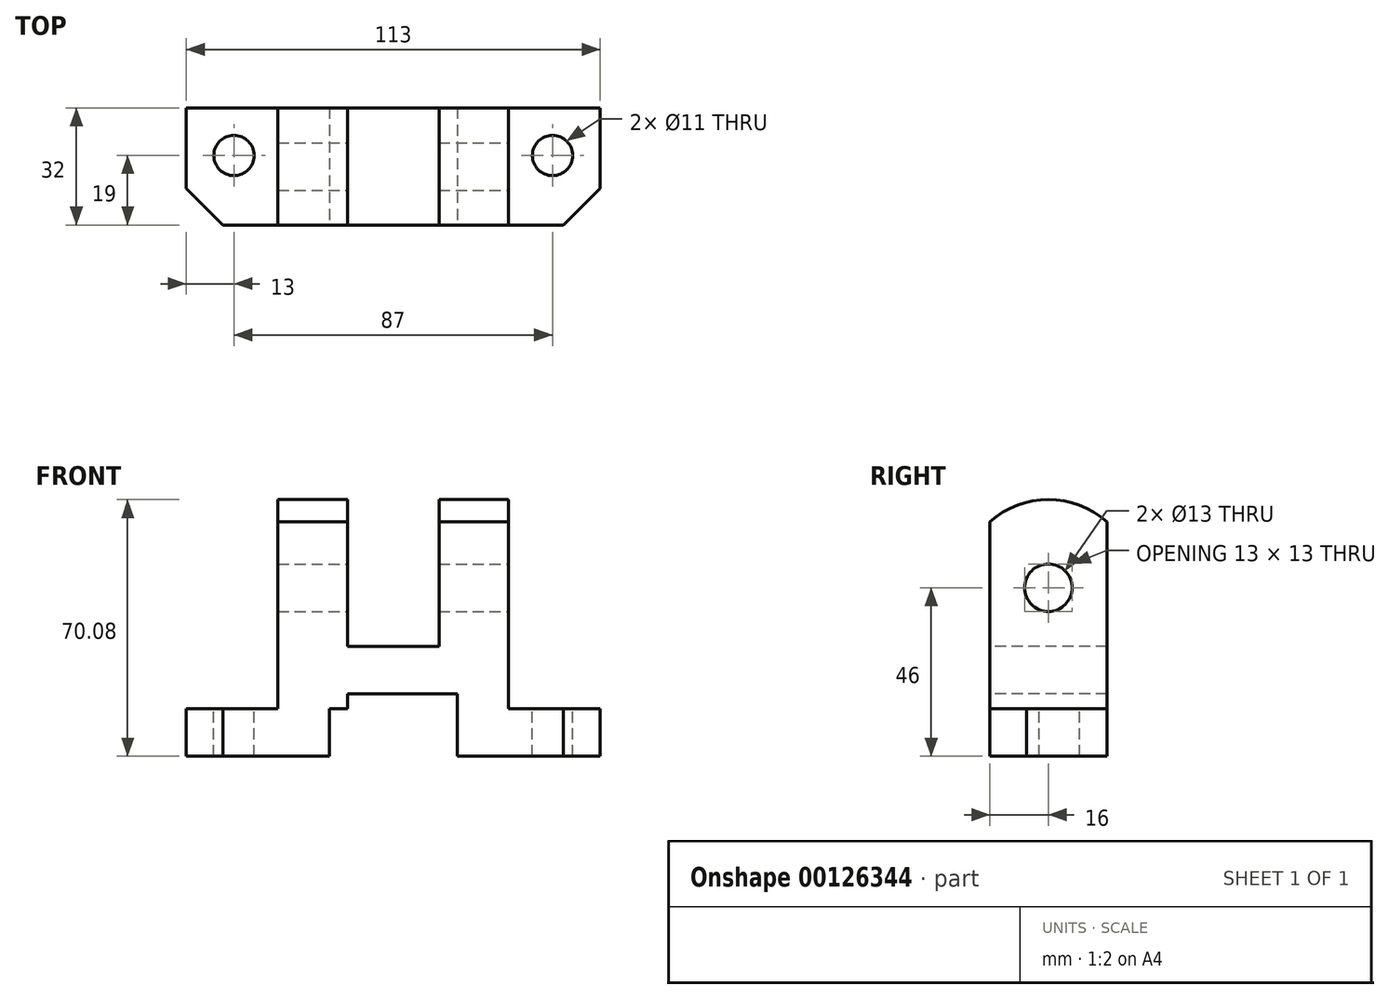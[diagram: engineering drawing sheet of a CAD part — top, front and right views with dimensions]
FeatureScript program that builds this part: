
annotation { "Feature Type Name" : "Feature", "Feature Type Description" : "" }
export const myFeature = defineFeature(function(context is Context, id is Id, definition is map)
    precondition{}
    {
        {
            var Q0;
            Q0=qCreatedBy(makeId("Front.planeOp"),FACE);
            var sketch = newSketch(context, id + "F0", { "sketchPlane" : qUnion([Q0])});
            skLineSegment(sketch, "E0", {"start": v(0, 0) * mm, "end": v(0, 13) * mm});
            skLineSegment(sketch, "E1", {"start": v(0, 13) * mm, "end": v(25, 13) * mm});
            skLineSegment(sketch, "E2", {"start": v(25, 13) * mm, "end": v(25, 64) * mm});
            skLineSegment(sketch, "E3", {"start": v(25, 64) * mm, "end": v(44, 64) * mm});
            skLineSegment(sketch, "E4", {"start": v(44, 64) * mm, "end": v(44, 30) * mm});
            skLineSegment(sketch, "E5", {"start": v(44, 30) * mm, "end": v(69, 30) * mm});
            skLineSegment(sketch, "E6", {"start": v(69, 30) * mm, "end": v(69, 64) * mm});
            skLineSegment(sketch, "E7", {"start": v(69, 64) * mm, "end": v(88, 64) * mm});
            skLineSegment(sketch, "E8", {"start": v(88, 64) * mm, "end": v(88, 13) * mm});
            skLineSegment(sketch, "E9", {"start": v(88, 13) * mm, "end": v(113, 13) * mm});
            skLineSegment(sketch, "E10", {"start": v(113, 13) * mm, "end": v(113, 0) * mm});
            skLineSegment(sketch, "E11", {"start": v(113, 0) * mm, "end": v(74, 0) * mm});
            skLineSegment(sketch, "E12", {"start": v(74, 0) * mm, "end": v(74, 17) * mm});
            skLineSegment(sketch, "E13", {"start": v(74, 17) * mm, "end": v(39, 17) * mm});
            skLineSegment(sketch, "E14", {"start": v(39, 17) * mm, "end": v(39, 0) * mm});
            skLineSegment(sketch, "E15", {"start": v(39, 0) * mm, "end": v(0, 0) * mm});
            skSolve(sketch);
        }
        {
            var Q0;
            Q0=makeQuery(id+"F0.imprint","IMPRINT",FACE,{"disambiguationData":[TD([[makeQuery(id+"F0.imprint","IMPRINT",EDGE,{"derivedFrom":sQuery(id+"F0.wireOp",EDGE,"E0")}),-1.0]])]});
            extrude(context, id + "F1", {"entities" : qUnion([Q0]), "oppositeDirection" : true, "depth" : 32 * mm});
        }
        {
            var Q0;
            Q0=makeQuery(id+"F1.opExtrude","SWEPT_FACE",FACE,{"disambiguationData":[OSD([sQuery(id+"F0.wireOp",EDGE,"E9")])]});
            var sketch = newSketch(context, id + "F2", { "sketchPlane" : qUnion([Q0])});
            skLineSegment(sketch, "E16", {"start": v(103, 0) * mm, "end": v(113, 10) * mm});
            skLineSegment(sketch, "E17", {"start": v(113, 10) * mm, "end": v(113, 0) * mm});
            skLineSegment(sketch, "E18", {"start": v(113, 0) * mm, "end": v(103, 0) * mm});
            skSolve(sketch);
        }
        {
            var Q0;
            Q0=makeQuery(id+"F2.imprint","IMPRINT",FACE,{"disambiguationData":[TD([[makeQuery(id+"F2.imprint","IMPRINT",EDGE,{"derivedFrom":sQuery(id+"F2.wireOp",EDGE,"E16")}),-1.0]])]});
            extrude(context, id + "F3", {"entities" : qUnion([Q0]), "operationType" : NewBodyOperationType.REMOVE, "endBound" : BoundingType.THROUGH_ALL, "oppositeDirection" : true, "depth" : 25 * mm});
        }
        {
            var Q0;
            Q0=makeQuery(id+"F1.opExtrude","SWEPT_FACE",FACE,{"disambiguationData":[OSD([sQuery(id+"F0.wireOp",EDGE,"E1")])]});
            var sketch = newSketch(context, id + "F4", { "sketchPlane" : qUnion([Q0])});
            skLineSegment(sketch, "E19", {"start": v(0, 0) * mm, "end": v(0, 10) * mm});
            skLineSegment(sketch, "E20", {"start": v(0, 10) * mm, "end": v(10, 0) * mm});
            skLineSegment(sketch, "E21", {"start": v(10, 0) * mm, "end": v(0, 0) * mm});
            skSolve(sketch);
        }
        {
            var Q0;
            Q0=makeQuery(id+"F4.imprint","IMPRINT",FACE,{"disambiguationData":[TD([[makeQuery(id+"F4.imprint","IMPRINT",EDGE,{"derivedFrom":sQuery(id+"F4.wireOp",EDGE,"E19")}),1.0]])]});
            extrude(context, id + "F5", {"entities" : qUnion([Q0]), "operationType" : NewBodyOperationType.REMOVE, "endBound" : BoundingType.THROUGH_ALL, "oppositeDirection" : true, "depth" : 25 * mm});
        }
        {
            var Q0;
            Q0=makeQuery(id+"F1.opExtrude","SWEPT_FACE",FACE,{"disambiguationData":[OSD([sQuery(id+"F0.wireOp",EDGE,"E9")])]});
            var sketch = newSketch(context, id + "F6", { "sketchPlane" : qUnion([Q0])});
            skCircle(sketch, "E22", {"center": v(100, 19) * mm, "radius": 5.5 * mm});
            skCircle(sketch, "E23", {"center": v(13, 19) * mm, "radius": 5.5 * mm});
            skSolve(sketch);
        }
        {
            var Q0;
            Q0=makeQuery(id+"F6.imprint","IMPRINT",FACE,{"disambiguationData":[TD([[makeQuery(id+"F6.imprint","IMPRINT",EDGE,{"derivedFrom":sQuery(id+"F6.wireOp",EDGE,"E23")}),1.0]])]});
            var Q1;
            Q1=makeQuery(id+"F6.imprint","IMPRINT",FACE,{"disambiguationData":[TD([[makeQuery(id+"F6.imprint","IMPRINT",EDGE,{"derivedFrom":sQuery(id+"F6.wireOp",EDGE,"E22")}),1.0]])]});
            extrude(context, id + "F7", {"entities" : qUnion([Q0, Q1]), "operationType" : NewBodyOperationType.REMOVE, "endBound" : BoundingType.THROUGH_ALL, "oppositeDirection" : true, "depth" : 25 * mm});
        }
        {
            var Q0;
            Q0=makeQuery(id+"F1.opExtrude","SWEPT_FACE",FACE,{"disambiguationData":[OSD([sQuery(id+"F0.wireOp",EDGE,"E8")])]});
            var sketch = newSketch(context, id + "F8", { "sketchPlane" : qUnion([Q0])});
            skArc(sketch, "E24", {"start": v(32, 64) * mm, "mid": v(16, 70.08) * mm, "end": v(0, 64) * mm});
            skSolve(sketch);
        }
        {
            var Q0;
            Q0=makeQuery(id+"F8.imprint","IMPRINT",FACE,{"disambiguationData":[TD([[makeQuery(id+"F8.imprint","IMPRINT",EDGE,{"derivedFrom":sQuery(id+"F8.wireOp",EDGE,"E24")}),1.0]])]});
            extrude(context, id + "F9", {"entities" : qUnion([Q0]), "operationType" : NewBodyOperationType.ADD, "oppositeDirection" : true, "depth" : 19 * mm});
        }
        {
            var Q0;
            Q0=makeQuery(id+"F1.opExtrude","SWEPT_FACE",FACE,{"disambiguationData":[OSD([sQuery(id+"F0.wireOp",EDGE,"E2")])]});
            var sketch = newSketch(context, id + "F10", { "sketchPlane" : qUnion([Q0])});
            skArc(sketch, "E25", {"start": v(0, 64) * mm, "mid": v(-16, 70.08) * mm, "end": v(-32, 64) * mm});
            skSolve(sketch);
        }
        {
            var Q0;
            Q0=makeQuery(id+"F10.imprint","IMPRINT",FACE,{"disambiguationData":[TD([[makeQuery(id+"F10.imprint","IMPRINT",EDGE,{"derivedFrom":sQuery(id+"F10.wireOp",EDGE,"E25")}),1.0]])]});
            extrude(context, id + "F11", {"entities" : qUnion([Q0]), "operationType" : NewBodyOperationType.ADD, "oppositeDirection" : true, "depth" : 19 * mm});
        }
        {
            var Q0;
            Q0=qCreatedBy(makeId("Right.planeOp"),FACE);
            cPlane(context, id + "F12", {"entities" : qUnion([Q0]), "cplaneType" : CPlaneType.OFFSET, "offset" : 100 * mm, "width" : 150 * mm, "height" : 150 * mm});
        }
        {
            var Q0;
            Q0=qCreatedBy(id+"F12.planeOp",FACE);
            var sketch = newSketch(context, id + "F13", { "sketchPlane" : qUnion([Q0])});
            skPoint(sketch, "E26.0", {"position": v(16, 46) * mm});
            skCircle(sketch, "E27", {"center": v(16, 46) * mm, "radius": 6.5 * mm});
            skSolve(sketch);
        }
        {
            var Q0;
            Q0=makeQuery(id+"F13.imprint","IMPRINT",FACE,{"disambiguationData":[TD([[makeQuery(id+"F13.imprint","IMPRINT",EDGE,{"derivedFrom":sQuery(id+"F13.wireOp",EDGE,"E27")}),1.0]])]});
            extrude(context, id + "F14", {"entities" : qUnion([Q0]), "operationType" : NewBodyOperationType.REMOVE, "endBound" : BoundingType.THROUGH_ALL, "oppositeDirection" : true, "depth" : 25 * mm});
        }
    });
